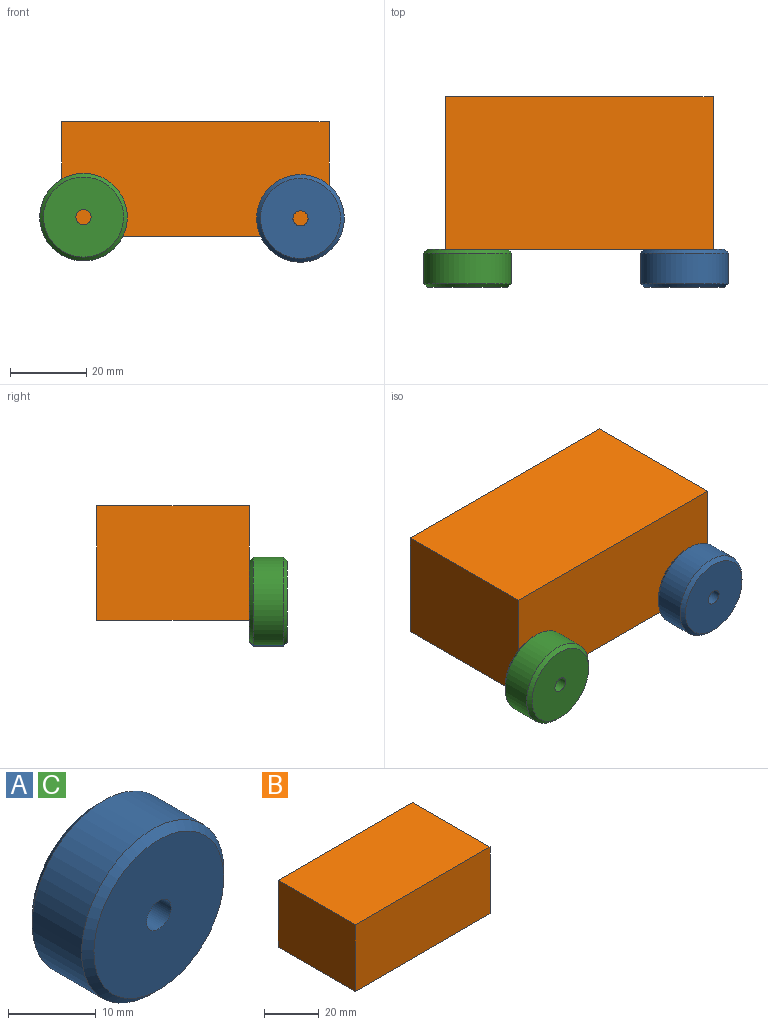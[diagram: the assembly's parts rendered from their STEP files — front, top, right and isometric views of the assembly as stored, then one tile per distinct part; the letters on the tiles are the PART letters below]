
ASSEMBLY  parts=3 mates=2
PART A: 10 faces, bbox 23x10x23 mm
  f0: plane 6.9x6.9mm, normal (0,1,0), area 25.1mm2, adj f4,f5
  f1: cylinder r=11.48mm len=22.95mm, axis (0,-1,0), area 573.2mm2, adj f8,f9
  f2: plane 20.95x20.95mm, normal (0,1,0), area 27.4mm2, adj f6,f8
  f3: plane 20.95x20.95mm, normal (0,-1,0), area 332.4mm2, adj f4,f9
  f4: cylinder r=1.98mm len=9.95mm, axis (0,-1,0), area 123.8mm2, adj f0,f3
  f5: cylinder r=3.45mm len=8.5mm, axis (0,1,0), area 184.3mm2, adj f0,f7
  f6: cylinder r=10.05mm len=20.1mm, axis (0,1,0), area 536.7mm2, adj f2,f7
  f7: plane 20.1x20.1mm, normal (0,1,0), area 279.9mm2, adj f5,f6
  f8: cone r=11.48mm half-angle=45deg, axis (0,-1,0), area 97.5mm2, adj f1,f2
  f9: cone r=10.47mm half-angle=45deg, axis (0,1,0), area 97.5mm2, adj f1,f3
PART B: 6 faces, bbox 70x40x30 mm
  f0: plane 70x30mm, normal (0,1,0), area 2100mm2, adj f1,f3,f4,f5
  f1: plane 70x40mm, normal (0,0,1), area 2800mm2, adj f0,f2,f4,f5
  f2: plane 70x30mm, normal (0,-1,0), area 2100mm2, adj f1,f3,f4,f5
  f3: plane 70x40mm, normal (0,0,-1), area 2800mm2, adj f0,f2,f4,f5
  f4: plane 40x30mm, normal (1,0,0), area 1200mm2, adj f0,f1,f2,f3
  f5: plane 40x30mm, normal (-1,0,0), area 1200mm2, adj f0,f1,f2,f3
PART C: same geometry as A
PLACE A t=(87.53,-40.14,-27.95)mm
PLACE B t=(25,-10.19,-17.66)mm
PLACE C t=(30.72,-40.14,-27.62)mm
MATE planar B.f2 <-> C.f5  axis (0,-1,0) through (60,-30.19,-17.66)mm
MATE planar B.f2 <-> A.f5  axis (0,-1,0) through (60,-30.19,-17.66)mm
